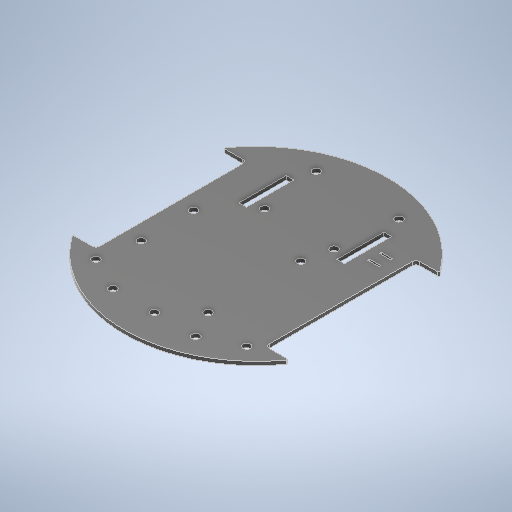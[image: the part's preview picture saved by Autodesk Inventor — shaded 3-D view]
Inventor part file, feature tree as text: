
AUTODESK INVENTOR PART (.ipt)
format: ipt  version: 2025.1 (Build 291241000, 241)  size: 496,640 bytes
history: native  units: mm
features: extrude x1, sketch x1
ambient origin geometry x8: Origin, YZ Plane, XZ Plane, XY Plane, X Axis, Y Axis, Z Axis, Center Point
bodies: Body1 (feature_tree)
feature tree (2):
  extrude  "Extrusão3"  Depth=0.5mm
  sketch  "Esboço1"  dims[d135=2.0mm d136=0.0mm d144=0.5mm d60=0.5mm d61=0.872665mm d62=0.5mm d63=0.872665mm]
